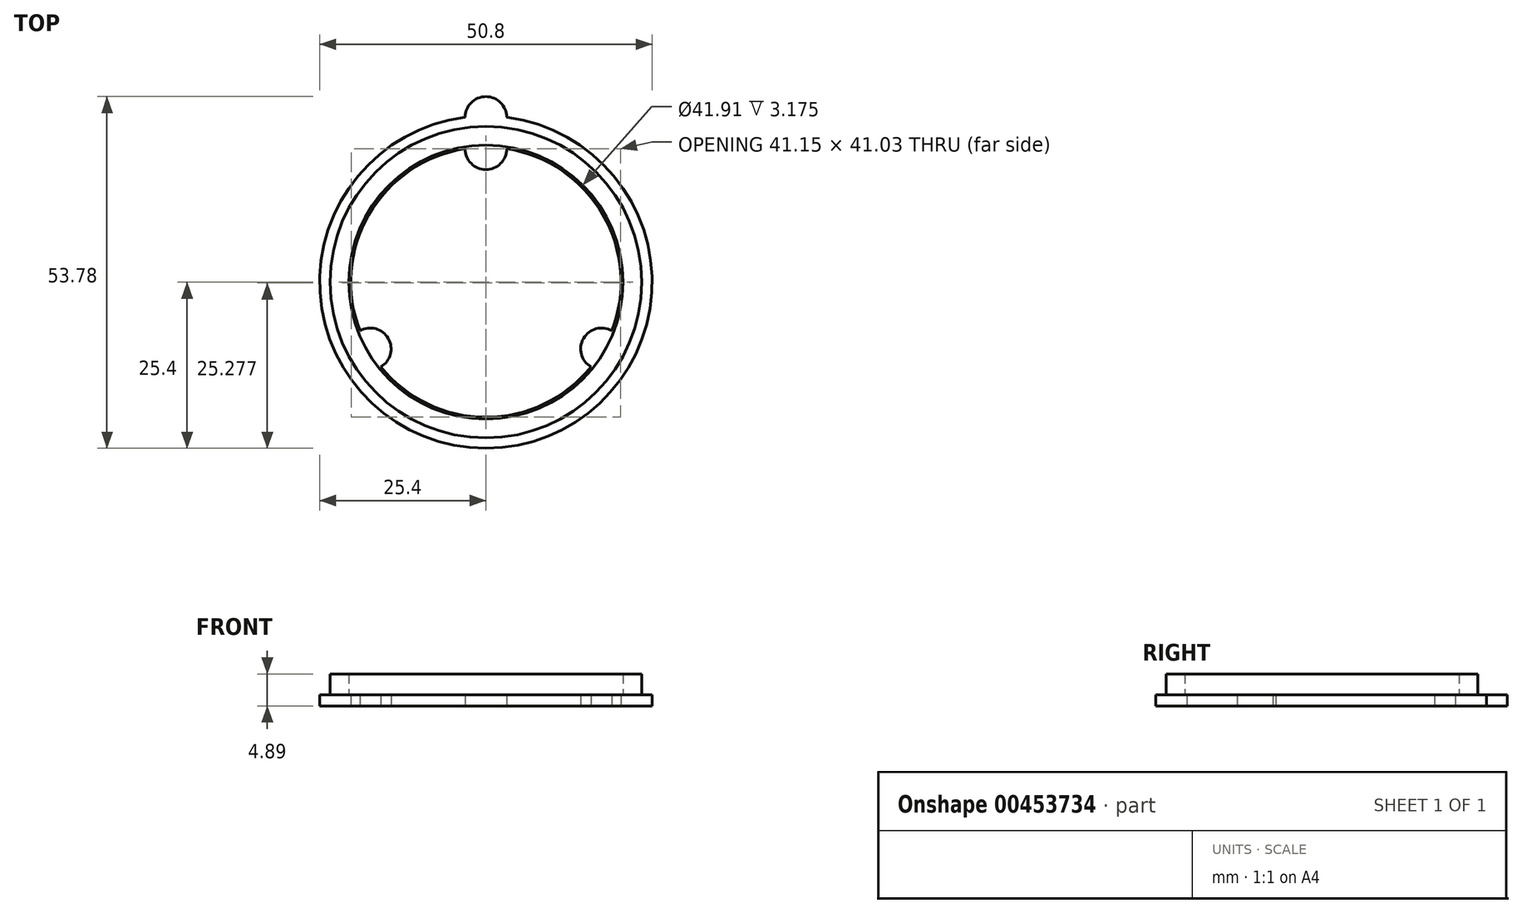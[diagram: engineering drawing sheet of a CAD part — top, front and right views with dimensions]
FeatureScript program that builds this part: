
annotation { "Feature Type Name" : "Feature", "Feature Type Description" : "" }
export const myFeature = defineFeature(function(context is Context, id is Id, definition is map)
    precondition{}
    {
        {
            var Q0;
            Q0=qCreatedBy(makeId("Top.planeOp"),FACE);
            var sketch = newSketch(context, id + "F0", { "sketchPlane" : qUnion([Q0])});
            skCircle(sketch, "E0", {"center": v(0, 0) * mm, "radius": 20.64 * mm});
            skCircle(sketch, "E1", {"center": v(0, 0) * mm, "radius": 25.4 * mm});
            skLineSegment(sketch, "E2", {"start": v(0, -25.4) * mm, "end": v(0, 55.74) * mm, "construction": true});
            skLineSegment(sketch, "E3", {"start": v(0, 0) * mm, "end": v(42.2, -24.37) * mm, "construction": true});
            skLineSegment(sketch, "E4", {"start": v(0, 0) * mm, "end": v(-46.37, -26.77) * mm, "construction": true});
            skLineSegment(sketch, "E5", {"start": v(-48.07, -24.09) * mm, "end": v(41.44, 27.6) * mm, "construction": true});
            skLineSegment(sketch, "E6.MirrorCS", {"start": v(-44.9, -29.59) * mm, "end": v(44.62, 22.1) * mm, "construction": true});
            skArc(sketch, "E7", {"start": v(-16.07, -12.95) * mm, "mid": v(-14.91, -8.6) * mm, "end": v(-19.25, -7.45) * mm});
            skLineSegment(sketch, "E8", {"start": v(3.17, 52.42) * mm, "end": v(3.18, -51.85) * mm, "construction": true});
            skLineSegment(sketch, "E9.MirrorCS", {"start": v(-3.17, 52.42) * mm, "end": v(-3.18, -51.85) * mm, "construction": true});
            skLineSegment(sketch, "E10", {"start": v(46.08, -22.94) * mm, "end": v(-34.55, 23.62) * mm, "construction": true});
            skLineSegment(sketch, "E11.MirrorCS", {"start": v(42.9, -28.44) * mm, "end": v(-37.73, 18.12) * mm, "construction": true});
            skArc(sketch, "E12", {"start": v(19.25, -7.45) * mm, "mid": v(14.91, -8.6) * mm, "end": v(16.07, -12.95) * mm});
            skArc(sketch, "E13", {"start": v(-3.18, 20.4) * mm, "mid": v(0, 17.22) * mm, "end": v(3.18, 20.4) * mm});
            skArc(sketch, "E14", {"start": v(3.18, 25.2) * mm, "mid": v(0, 28.38) * mm, "end": v(-3.18, 25.2) * mm});
            skSolve(sketch);
        }
        {
            var Q0;
            {var subQ0=sQuery(id+"F0.wireOp",EDGE,"E13");Q0=makeQuery(id+"F0.imprint","IMPRINT",FACE,{"disambiguationData":[TD([[makeQuery(id+"F0.imprint","IMPRINT",EDGE,{"derivedFrom":subQ0}),1.0]])]});}
            var Q1;
            {var subQ0=sQuery(id+"F0.wireOp",EDGE,"E7");Q1=makeQuery(id+"F0.imprint","IMPRINT",FACE,{"disambiguationData":[TD([[makeQuery(id+"F0.imprint","IMPRINT",EDGE,{"derivedFrom":subQ0}),1.0]])]});}
            var Q2;
            {var subQ0=sQuery(id+"F0.wireOp",EDGE,"E12");Q2=makeQuery(id+"F0.imprint","IMPRINT",FACE,{"disambiguationData":[TD([[makeQuery(id+"F0.imprint","IMPRINT",EDGE,{"derivedFrom":subQ0}),1.0]])]});}
            var Q3;
            Q3=makeQuery(id+"F0.imprint","IMPRINT",FACE,{"disambiguationData":[TD([[makeQuery(id+"F0.imprint","IMPRINT",EDGE,{"derivedFrom":sQuery(id+"F0.wireOp",EDGE,"E1")}),1.0]])]});
            var Q4;
            {var subQ0=sQuery(id+"F0.wireOp",EDGE,"E14");Q4=makeQuery(id+"F0.imprint","IMPRINT",FACE,{"disambiguationData":[TD([[makeQuery(id+"F0.imprint","IMPRINT",EDGE,{"derivedFrom":subQ0}),1.0]])]});}
            extrude(context, id + "F1", {"entities" : qUnion([Q0, Q1, Q2, Q3, Q4]), "depth" : 1.71 * mm});
        }
        {
            var Q0;
            Q0=makeQuery(id+"F1.opExtrude","CAP_FACE",FACE,{"disambiguationData":[OSD([sQuery(id+"F0.wireOp",EDGE,"E0"),sQuery(id+"F0.wireOp",EDGE,"E1"),sQuery(id+"F0.wireOp",EDGE,"E7"),sQuery(id+"F0.wireOp",EDGE,"E12"),sQuery(id+"F0.wireOp",EDGE,"E13")])],"isStart":false});
            var sketch = newSketch(context, id + "F2", { "sketchPlane" : qUnion([Q0])});
            skCircle(sketch, "E15", {"center": v(0, 0) * mm, "radius": 20.96 * mm});
            skCircle(sketch, "E16", {"center": v(0, 0) * mm, "radius": 23.81 * mm});
            skSolve(sketch);
        }
        {
            var Q0;
            Q0=makeQuery(id+"F2.imprint","IMPRINT",FACE,{"disambiguationData":[TD([[makeQuery(id+"F2.imprint","IMPRINT",EDGE,{"derivedFrom":sQuery(id+"F2.wireOp",EDGE,"E15")}),-1.0]])]});
            extrude(context, id + "F3", {"entities" : qUnion([Q0]), "operationType" : NewBodyOperationType.ADD, "depth" : 3.17 * mm});
        }
    });
